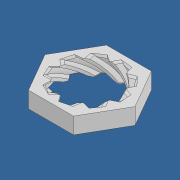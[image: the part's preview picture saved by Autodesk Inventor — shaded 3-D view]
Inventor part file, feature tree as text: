
AUTODESK INVENTOR PART (.ipt)
format: ipt  version: 2022.5 (Build 265521000, 521)  size: 1,147,904 bytes
history: native  units: mm
features: chamfer x2, sketch x2, other x1, extrude x1, helix x1, pattern_circular x1
ambient origin geometry x8: Origin, YZ Plane, XZ Plane, XY Plane, X Axis, Y Axis, Z Axis, Center Point
bodies: Body1 (feature_tree)
feature tree (8):
  other  "實體1"
  extrude  "擠出1"  Depth=6.976mm
  helix  "螺旋1"  [1 undecoded]
  pattern_circular  "環形陣列1"  [2 undecoded]
  chamfer  "倒角1"  Distance=90.0mm
  chamfer  "倒角2"  Distance=70.0mm
  sketch  "草圖1"
  sketch  "草圖2"
note: 3 required parameter values undecoded (feature->parameter linkage not recoverable at this tier; creation-order binding heuristic only, values carry confidence <= 0.55)
